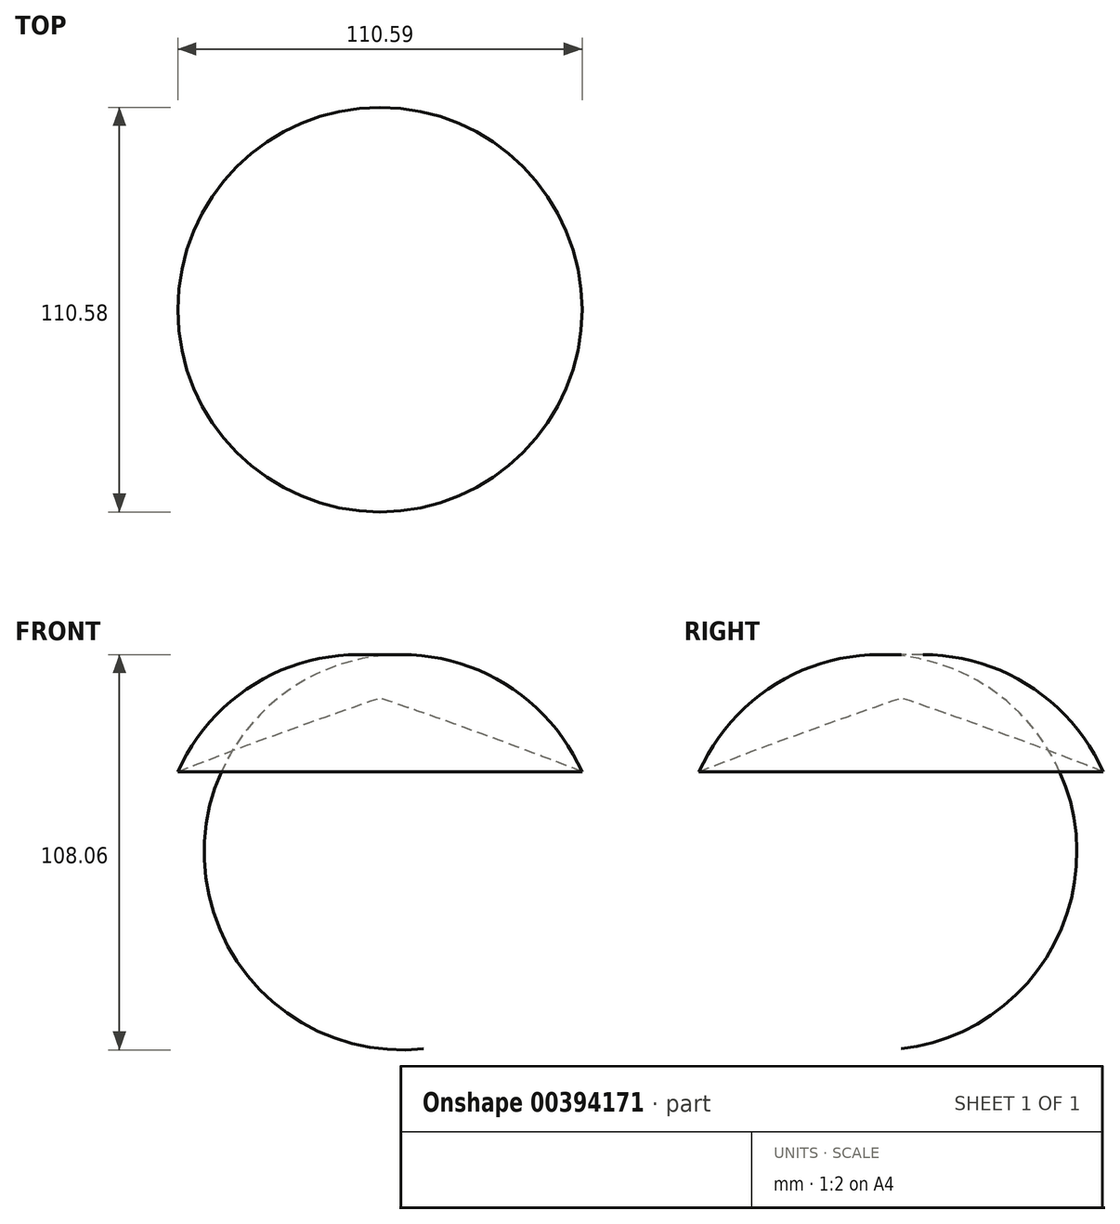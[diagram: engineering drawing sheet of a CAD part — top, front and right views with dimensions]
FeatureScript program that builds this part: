
annotation { "Feature Type Name" : "Feature", "Feature Type Description" : "" }
export const myFeature = defineFeature(function(context is Context, id is Id, definition is map)
    precondition{}
    {
        {
            var Q0;
            Q0=qCreatedBy(makeId("Front.planeOp"),FACE);
            var sketch = newSketch(context, id + "F0", { "sketchPlane" : qUnion([Q0])});
            skLineSegment(sketch, "E0", {"start": v(-20.5, 52.22) * mm, "end": v(-20.5, -55.18) * mm});
            skArc(sketch, "E1", {"start": v(-20.5, -55.18) * mm, "mid": v(39.49, -1.48) * mm, "end": v(-20.5, 52.22) * mm});
            skLineSegment(sketch, "E2.bottom", {"start": v(-10.81, 18.6) * mm, "end": v(28.14, 18.6) * mm});
            skLineSegment(sketch, "E2.top", {"start": v(-10.81, -31.1) * mm, "end": v(28.14, -31.1) * mm});
            skLineSegment(sketch, "E2.left", {"start": v(-10.81, 18.6) * mm, "end": v(-10.81, -31.1) * mm});
            skLineSegment(sketch, "E2.right", {"start": v(28.14, 18.6) * mm, "end": v(28.14, -31.1) * mm});
            skEllipse(sketch, "E3", {"center": v(-18.46, 33.47) * mm, "majorRadius": 99.01 * mm, "minorRadius": 6.18 * mm, "majorAxis": v(0.95, -0.33)});
            skSolve(sketch);
        }
        {
            var Q0;
            Q0=makeQuery(id+"F0.imprint","IMPRINT",FACE,{"disambiguationData":[TD([[makeQuery(id+"F0.imprint","IMPRINT",EDGE,{"derivedFrom":sQuery(id+"F0.wireOp",EDGE,"E0")}),1.0]])]});
            var Q1;
            Q1=sQuery(id+"F0.wireOp",EDGE,"E0");
            revolve(context, id + "F1", {"entities" : qUnion([Q0]), "axis" : qUnion([Q1]), "revolveType" : RevolveType.FULL});
        }
    });
